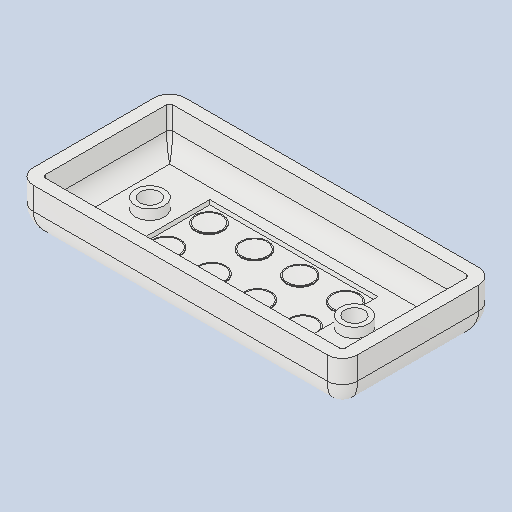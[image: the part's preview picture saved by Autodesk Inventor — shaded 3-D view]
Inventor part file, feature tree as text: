
AUTODESK INVENTOR PART (.ipt)
format: ipt  version: 2023.4 (Build 274418000, 418)  size: 215,552 bytes
history: native  units: in
note: dims shown in document units (in); Inventor stores cm internally (conversion verified against a paired STEP export)
features: fillet x1
ambient origin geometry x8: Origin, YZ Plane, XZ Plane, XY Plane, X Axis, Y Axis, Z Axis, Center Point
bodies: Solid1 (feature_tree)
feature tree (1):
  fillet  "Fillet12"  [1 undecoded]
note: 1 required parameter value undecoded (feature->parameter linkage not recoverable at this tier; creation-order binding heuristic only, values carry confidence <= 0.55)
